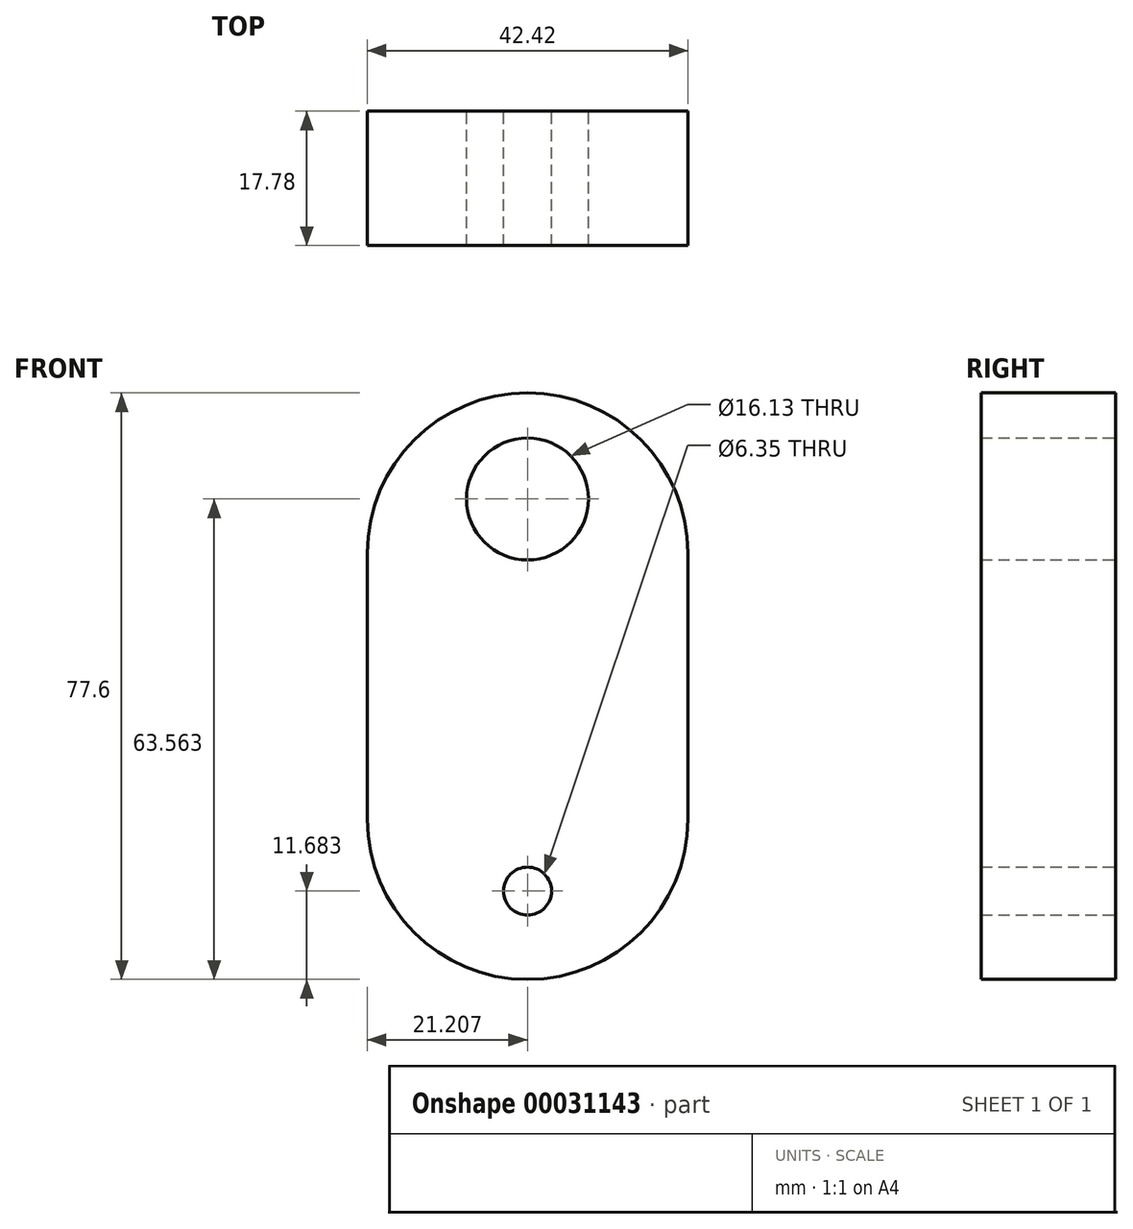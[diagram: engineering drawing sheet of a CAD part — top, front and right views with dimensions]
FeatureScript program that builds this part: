
annotation { "Feature Type Name" : "Feature", "Feature Type Description" : "" }
export const myFeature = defineFeature(function(context is Context, id is Id, definition is map)
    precondition{}
    {
        {
            var Q0;
            Q0=qCreatedBy(makeId("Front.planeOp"),FACE);
            var sketch = newSketch(context, id + "F0", { "sketchPlane" : qUnion([Q0])});
            skLineSegment(sketch, "E0.bottom", {"start": v(-61.63, 3.04) * mm, "end": v(-19.21, 3.04) * mm});
            skLineSegment(sketch, "E0.top", {"start": v(-61.63, -32.14) * mm, "end": v(-19.21, -32.14) * mm});
            skLineSegment(sketch, "E0.left", {"start": v(-61.63, 3.04) * mm, "end": v(-61.63, -32.14) * mm});
            skLineSegment(sketch, "E0.right", {"start": v(-19.21, 3.04) * mm, "end": v(-19.21, -32.14) * mm});
            skArc(sketch, "E1", {"start": v(-19.21, 3.04) * mm, "mid": v(-40.42, 24.25) * mm, "end": v(-61.63, 3.04) * mm});
            skCircle(sketch, "E2", {"center": v(-40.42, 10.21) * mm, "radius": 8.06 * mm});
            skArc(sketch, "E3", {"start": v(-61.63, -32.14) * mm, "mid": v(-40.42, -53.35) * mm, "end": v(-19.21, -32.14) * mm});
            skCircle(sketch, "E4", {"center": v(-40.42, -41.67) * mm, "radius": 3.18 * mm});
            skSolve(sketch);
        }
        {
            var Q0;
            Q0 = qSketchRegion(id + "F0", true);
            extrude(context, id + "F1", {"entities" : qUnion([Q0]), "depth" : 17.78 * mm});
        }
    });
